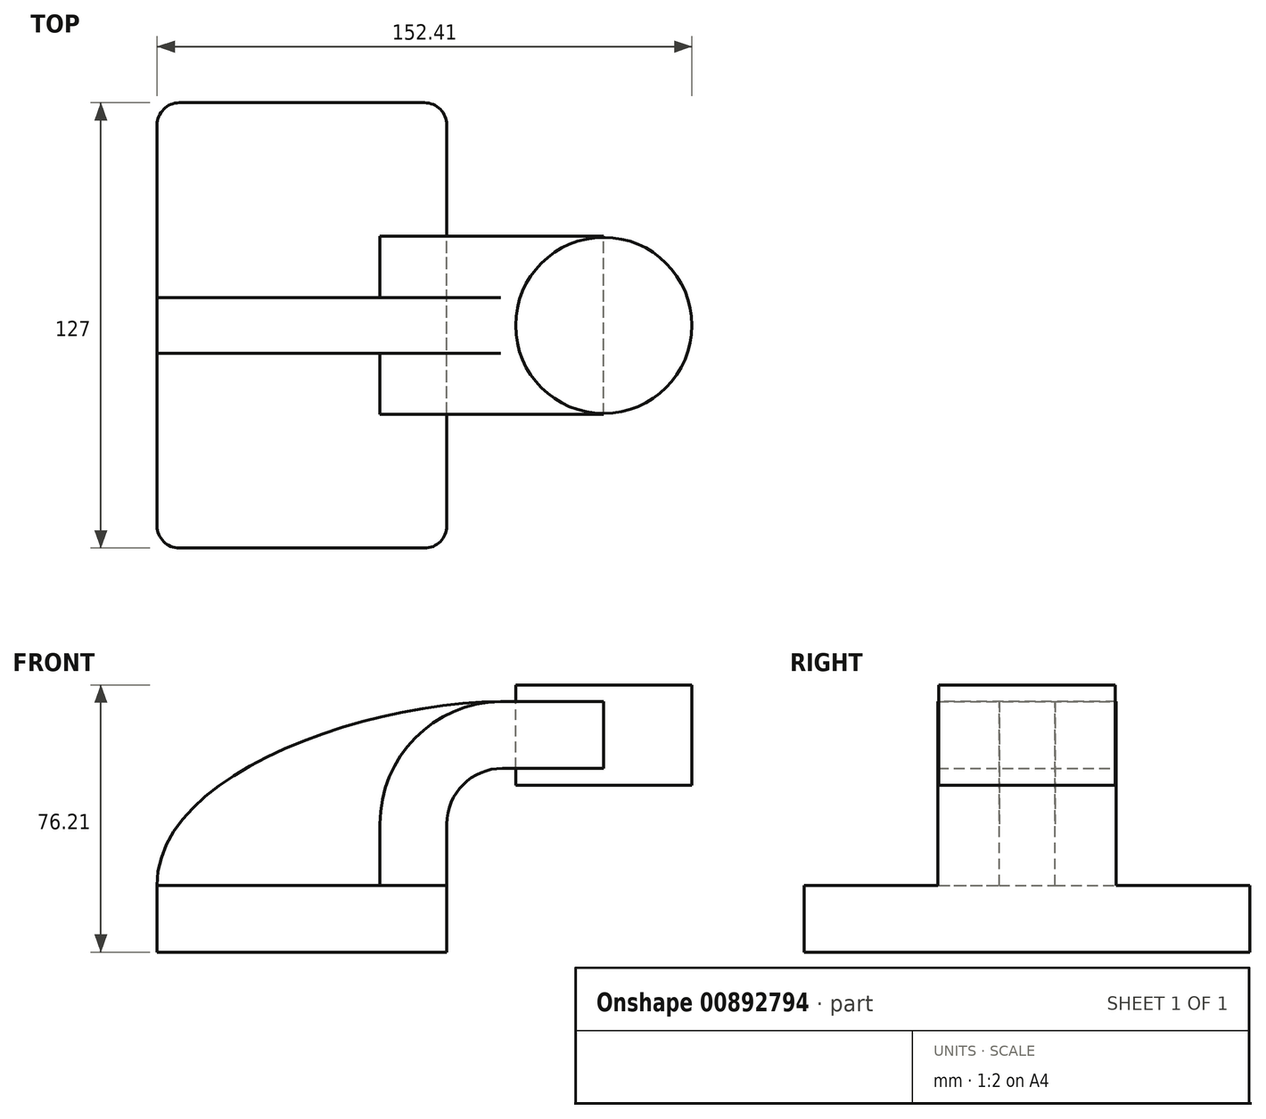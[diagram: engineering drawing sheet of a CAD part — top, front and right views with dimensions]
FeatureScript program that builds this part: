
annotation { "Feature Type Name" : "Feature", "Feature Type Description" : "" }
export const myFeature = defineFeature(function(context is Context, id is Id, definition is map)
    precondition{}
    {
        {
            var Q0;
            Q0=qCreatedBy(makeId("Front.planeOp"),FACE);
            var sketch = newSketch(context, id + "F0", { "sketchPlane" : qUnion([Q0])});
            skLineSegment(sketch, "E0.bottom", {"start": v(41.28, -9.52) * mm, "end": v(-41.28, -9.53) * mm});
            skLineSegment(sketch, "E0.top", {"start": v(41.28, 9.53) * mm, "end": v(-41.28, 9.53) * mm});
            skLineSegment(sketch, "E0.left", {"start": v(41.28, -9.52) * mm, "end": v(41.27, 9.53) * mm});
            skLineSegment(sketch, "E0.right", {"start": v(-41.28, -9.53) * mm, "end": v(-41.28, 9.53) * mm});
            skPoint(sketch, "E0.middle", {"position": v(0, 0) * mm});
            skLineSegment(sketch, "E1.bottom", {"start": v(60.32, 38.1) * mm, "end": v(111.12, 38.1) * mm});
            skLineSegment(sketch, "E1.top", {"start": v(60.32, 66.68) * mm, "end": v(111.12, 66.68) * mm});
            skLineSegment(sketch, "E1.left", {"start": v(60.32, 38.1) * mm, "end": v(60.32, 66.67) * mm});
            skLineSegment(sketch, "E1.right", {"start": v(111.12, 38.1) * mm, "end": v(111.12, 66.68) * mm});
            skPoint(sketch, "E1.middle", {"position": v(85.72, 52.39) * mm});
            skLineSegment(sketch, "E2", {"start": v(41.28, 9.53) * mm, "end": v(41.28, 27) * mm});
            skArc(sketch, "E3", {"start": v(41.27, 27) * mm, "mid": v(45.92, 38.23) * mm, "end": v(57.15, 42.88) * mm});
            skLineSegment(sketch, "E4", {"start": v(57.15, 42.88) * mm, "end": v(86, 42.88) * mm});
            skLineSegment(sketch, "E5.0", {"start": v(57.15, 61.93) * mm, "end": v(86, 61.93) * mm});
            skArc(sketch, "E5.1", {"start": v(22.23, 27) * mm, "mid": v(32.45, 51.7) * mm, "end": v(57.15, 61.93) * mm});
            skLineSegment(sketch, "E5.2", {"start": v(22.22, 9.53) * mm, "end": v(22.22, 27) * mm});
            skLineSegment(sketch, "E6", {"start": v(86, 61.93) * mm, "end": v(86, 42.88) * mm});
            skFitSpline(sketch, "E7", {"points": [v(-41.28, 9.53) * mm, v(57.15, 61.93) * mm], "startDerivative": vector(-1.18, 93.77) * mm, "endDerivative": vector(120.92, 0.62) * mm});
            skLineSegment(sketch, "E8", {"start": v(86, 66.68) * mm, "end": v(86, 38.1) * mm});
            skSolve(sketch);
        }
        {
            var Q0;
            Q0=makeQuery(id+"F0.imprint","IMPRINT",FACE,{"disambiguationData":[TD([[makeQuery(id+"F0.imprint","IMPRINT",EDGE,{"derivedFrom":sQuery(id+"F0.wireOp",EDGE,"E0.bottom")}),-1.0]])]});
            extrude(context, id + "F1", {"entities" : qUnion([Q0]), "endBound" : BoundingType.SYMMETRIC, "depth" : 127 * mm, "offsetDistance" : 25.4 * mm});
        }
        {
            var Q0;
            {var subQ1=sQuery(id+"F0.wireOp",EDGE,"E2");Q0=makeQuery(id+"F0.imprint","IMPRINT",FACE,{"disambiguationData":[TD([[makeQuery(id+"F0.imprint","IMPRINT",EDGE,{"derivedFrom":subQ1}),1.0]])]});}
            var Q1;
            {var subQ5=sQuery(id+"F0.wireOp",EDGE,"E6");Q1=makeQuery(id+"F0.imprint","IMPRINT",FACE,{"disambiguationData":[TD([[makeQuery(id+"F0.imprint","IMPRINT",EDGE,{"derivedFrom":subQ5}),-1.0]])]});}
            var Q2;
            {var subQ0=sQuery(id+"F0.wireOp",EDGE,"E4");var subQ1=sQuery(id+"F0.wireOp",EDGE,"E1.left");var subQ2=makeQuery(id+"F0.imprint","INTERSECT",VERTEX,{"derivedFrom":[subQ1,subQ0]});Q2=makeQuery(id+"F0.imprint","IMPRINT",FACE,{"disambiguationData":[TD([[makeQuery(id+"F0.imprint","IMPRINT",EDGE,{"disambiguationData":[TD([[subQ2,-1.0]])],"derivedFrom":subQ1}),-1.0]])]});}
            extrude(context, id + "F2", {"entities" : qUnion([Q0, Q1, Q2]), "operationType" : NewBodyOperationType.ADD, "endBound" : BoundingType.SYMMETRIC, "depth" : 50.8 * mm, "offsetDistance" : 25.4 * mm});
        }
        {
            var Q0;
            {var subQ3=sQuery(id+"F0.wireOp",EDGE,"E5.2");Q0=makeQuery(id+"F0.imprint","IMPRINT",FACE,{"disambiguationData":[TD([[makeQuery(id+"F0.imprint","IMPRINT",EDGE,{"derivedFrom":subQ3}),1.0]])]});}
            extrude(context, id + "F3", {"entities" : qUnion([Q0]), "operationType" : NewBodyOperationType.ADD, "endBound" : BoundingType.SYMMETRIC, "depth" : 15.88 * mm, "offsetDistance" : 25.4 * mm});
        }
        {
            var Q0;
            {var subQ4=sQuery(id+"F0.wireOp",EDGE,"E1.right");Q0=makeQuery(id+"F0.imprint","IMPRINT",FACE,{"disambiguationData":[TD([[makeQuery(id+"F0.imprint","IMPRINT",EDGE,{"derivedFrom":subQ4}),1.0]])]});}
            var Q1;
            Q1=sQuery(id+"F0.wireOp",EDGE,"E6");
            revolve(context, id + "F4", {"surfaceOperationType" : NewSurfaceOperationType.NEW, "entities" : qUnion([Q0]), "axis" : qUnion([Q1]), "revolveType" : RevolveType.FULL});
        }
        {
            var Q0;
            Q0=makeQuery(id+"F1.opExtrude","CAP_EDGE",EDGE,{"disambiguationData":[OSD([sQuery(id+"F0.wireOp",EDGE,"E0.left")])],"isStart":false});
            var Q1;
            Q1=makeQuery(id+"F1.opExtrude","CAP_EDGE",EDGE,{"disambiguationData":[OSD([sQuery(id+"F0.wireOp",EDGE,"E0.right")])],"isStart":false});
            var Q2;
            Q2=makeQuery(id+"F1.opExtrude","CAP_EDGE",EDGE,{"disambiguationData":[OSD([sQuery(id+"F0.wireOp",EDGE,"E0.left")])],"isStart":true});
            var Q3;
            Q3=makeQuery(id+"F1.opExtrude","CAP_EDGE",EDGE,{"disambiguationData":[OSD([sQuery(id+"F0.wireOp",EDGE,"E0.right")])],"isStart":true});
            fillet(context, id + "F5", {"entities" : qUnion([Q0, Q1, Q2, Q3]), "radius" : 6.35 * mm, "tangentPropagation" : true, "allowEdgeOverflow" : false});
        }
    });
